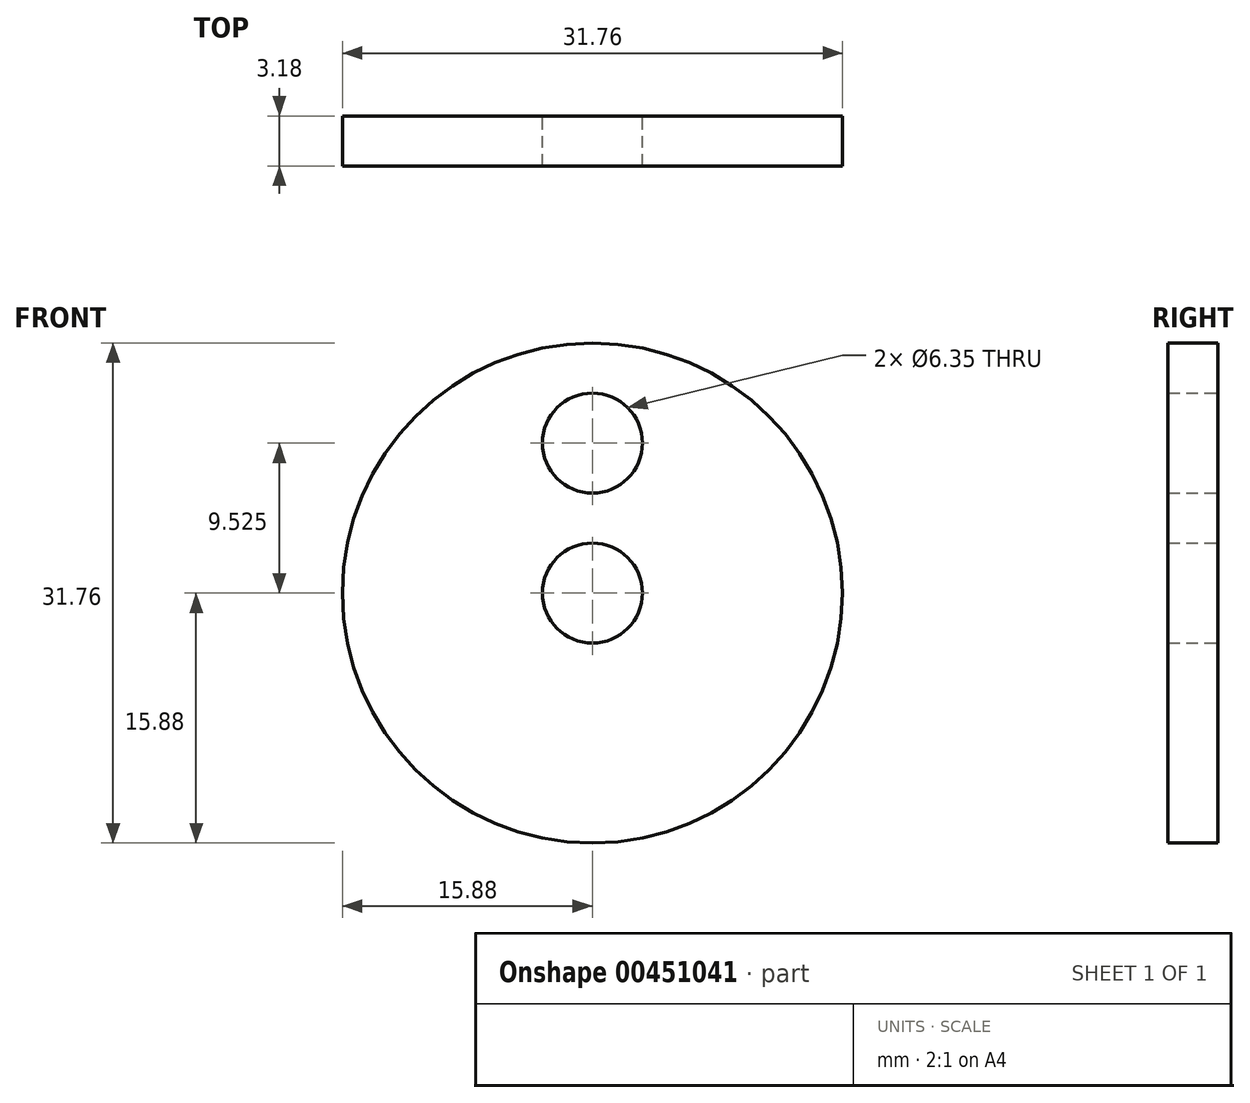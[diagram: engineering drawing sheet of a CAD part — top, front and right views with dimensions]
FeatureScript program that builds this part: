
annotation { "Feature Type Name" : "Feature", "Feature Type Description" : "" }
export const myFeature = defineFeature(function(context is Context, id is Id, definition is map)
    precondition{}
    {
        {
            var Q0;
            Q0=qCreatedBy(makeId("Front.planeOp"),FACE);
            var sketch = newSketch(context, id + "F0", { "sketchPlane" : qUnion([Q0])});
            skCircle(sketch, "E0", {"center": v(0, 0) * mm, "radius": 15.88 * mm});
            skCircle(sketch, "E1", {"center": v(0, 0) * mm, "radius": 3.18 * mm});
            skLineSegment(sketch, "E2", {"start": v(0, 3.18) * mm, "end": v(0, 15.88) * mm, "construction": true});
            skCircle(sketch, "E3", {"center": v(0, 9.53) * mm, "radius": 3.18 * mm});
            skSolve(sketch);
        }
        {
            var Q0;
            Q0 = qSketchRegion(id + "F0", true);
            extrude(context, id + "F1", {"entities" : qUnion([Q0]), "depth" : 3.17 * mm});
        }
    });
